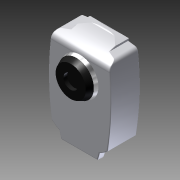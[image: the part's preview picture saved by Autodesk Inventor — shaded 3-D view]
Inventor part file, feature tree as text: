
AUTODESK INVENTOR PART (.ipt)
format: ipt  version: 2011 (Build 150239000, 239)  size: 357,888 bytes
history: native  units: in
note: dims shown in document units (in); Inventor stores cm internally (conversion verified against a paired STEP export)
features: extrude x5, sketch x5, plane x3, other x3, fillet x1
ambient origin geometry x8: Origin, YZ Plane, XZ Plane, XY Plane, X Axis, Y Axis, Z Axis, Center Point
bodies: Solid1 (feature_tree)
feature tree (17):
  extrude  "Extrusion1"  Depth=0.125in
  extrude  "Extrusion2"  Depth=3.0in TaperAngle=0.0deg
  fillet  "Fillet1"  Radius=0.0312in
  extrude  "Extrusion4"  Depth=0.1875in
  extrude  "Extrusion5"  [1 undecoded]
  extrude  "Extrusion6"  [1 undecoded]
  plane  "Work Plane1"
  other  "Work Axis1"
  sketch  "Sketch1"  dims[d2=7.1396in d7=0.125in]
  other  "Image1"
  sketch  "Sketch2"  dims[d47=1.34in d48=0.0in d108=3.0in d109=0.0in d110=0.0312in]
  other  "Image2"
  sketch  "Sketch5"  dims[d113=0.125in d114=-0.1031in d115=0.1875in d116=-0.1718in]
  sketch  "Sketch6"  dims[d117=0.125in d118=0.0in]
  sketch  "Sketch7"
  plane  "Work Plane2"
  plane  "Work Plane3"
note: 2 required parameter values undecoded (feature->parameter linkage not recoverable at this tier; creation-order binding heuristic only, values carry confidence <= 0.55)
